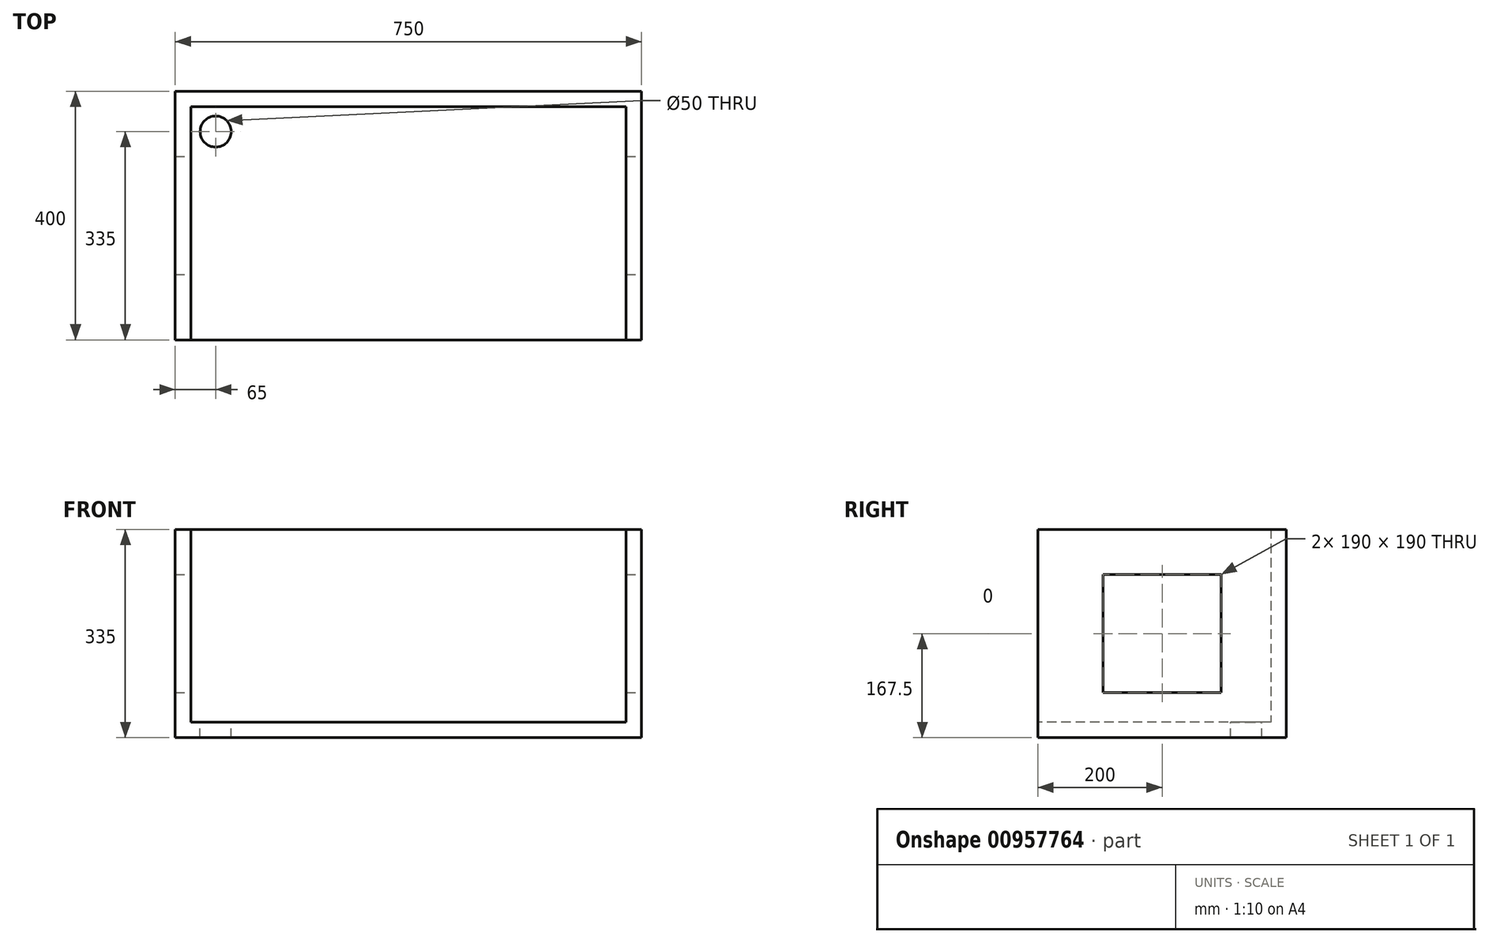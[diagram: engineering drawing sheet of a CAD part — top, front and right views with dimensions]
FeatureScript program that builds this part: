
annotation { "Feature Type Name" : "Feature", "Feature Type Description" : "" }
export const myFeature = defineFeature(function(context is Context, id is Id, definition is map)
    precondition{}
    {
        {
            var Q0;
            Q0=qCreatedBy(makeId("Top.planeOp"),FACE);
            var sketch = newSketch(context, id + "F0", { "sketchPlane" : qUnion([Q0])});
            skLineSegment(sketch, "E0.bottom", {"start": v(-375, 200) * mm, "end": v(375, 200) * mm});
            skLineSegment(sketch, "E0.top", {"start": v(-375, -200) * mm, "end": v(375, -200) * mm});
            skLineSegment(sketch, "E0.left", {"start": v(-375, 200) * mm, "end": v(-375, -200) * mm});
            skLineSegment(sketch, "E0.right", {"start": v(375, 200) * mm, "end": v(375, -200) * mm});
            skPoint(sketch, "E0.middle", {"position": v(0, 0) * mm});
            skSolve(sketch);
        }
        {
            var Q0;
            Q0=makeQuery(id+"F0.imprint","IMPRINT",FACE,{"disambiguationData":[TD([[makeQuery(id+"F0.imprint","IMPRINT",EDGE,{"derivedFrom":sQuery(id+"F0.wireOp",EDGE,"E0.bottom")}),-1.0]])]});
            extrude(context, id + "F1", {"entities" : qUnion([Q0]), "depth" : 25 * mm, "offsetDistance" : 25 * mm});
        }
        {
            var Q0;
            Q0=makeQuery(id+"F1.opExtrude","CAP_FACE",FACE,{"disambiguationData":[OSD([sQuery(id+"F0.wireOp",EDGE,"E0.bottom"),sQuery(id+"F0.wireOp",EDGE,"E0.top"),sQuery(id+"F0.wireOp",EDGE,"E0.left"),sQuery(id+"F0.wireOp",EDGE,"E0.right")])],"isStart":false});
            var sketch = newSketch(context, id + "F2", { "sketchPlane" : qUnion([Q0])});
            skLineSegment(sketch, "E1.0", {"start": v(-350, 175) * mm, "end": v(-350, -200) * mm});
            skLineSegment(sketch, "E2.0", {"start": v(-350, 175) * mm, "end": v(350, 175) * mm});
            skLineSegment(sketch, "E3.0", {"start": v(350, 175) * mm, "end": v(350, -200) * mm});
            skSolve(sketch);
        }
        {
            var Q0;
            {var subQ1=sQuery(id+"F2.wireOp",EDGE,"E1.0");Q0=makeQuery(id+"F2.imprint","IMPRINT",FACE,{"disambiguationData":[TD([[makeQuery(id+"F2.imprint","IMPRINT",EDGE,{"derivedFrom":subQ1}),-1.0]])]});}
            extrude(context, id + "F3", {"entities" : qUnion([Q0]), "operationType" : NewBodyOperationType.ADD, "depth" : 310 * mm, "offsetDistance" : 25 * mm});
        }
        {
            var Q0;
            {var subQ0=sQuery(id+"F0.wireOp",EDGE,"E0.right");Q0=makeQuery(id+"F3.boolean.opBoolean","MERGE",FACE,{"derivedFrom":[makeQuery(id+"F1.opExtrude","SWEPT_FACE",FACE,{"disambiguationData":[OSD([subQ0])]}),makeQuery(id+"F3.opExtrude","SWEPT_FACE",FACE,{"disambiguationData":[OSD([subQ0])]})]});}
            var sketch = newSketch(context, id + "F4", { "sketchPlane" : qUnion([Q0])});
            skLineSegment(sketch, "E4", {"start": v(-200, 335) * mm, "end": v(200, 0) * mm, "construction": true});
            skLineSegment(sketch, "E5.bottom", {"start": v(-95, 262.5) * mm, "end": v(95, 262.5) * mm});
            skLineSegment(sketch, "E5.top", {"start": v(-95, 72.5) * mm, "end": v(95, 72.5) * mm});
            skLineSegment(sketch, "E5.left", {"start": v(-95, 262.5) * mm, "end": v(-95, 72.5) * mm});
            skLineSegment(sketch, "E5.right", {"start": v(95, 262.5) * mm, "end": v(95, 72.5) * mm});
            skPoint(sketch, "E5.middle", {"position": v(0, 167.5) * mm});
            skSolve(sketch);
        }
        {
            var Q0;
            Q0=makeQuery(id+"F4.imprint","IMPRINT",FACE,{"disambiguationData":[TD([[makeQuery(id+"F4.imprint","IMPRINT",EDGE,{"derivedFrom":sQuery(id+"F4.wireOp",EDGE,"E5.bottom")}),-1.0]])]});
            extrude(context, id + "F5", {"entities" : qUnion([Q0]), "operationType" : NewBodyOperationType.REMOVE, "endBound" : BoundingType.THROUGH_ALL, "oppositeDirection" : true, "depth" : 25 * mm, "offsetDistance" : 25 * mm});
        }
        {
            var Q0;
            Q0=makeQuery(id+"F1.opExtrude","CAP_FACE",FACE,{"disambiguationData":[OSD([sQuery(id+"F0.wireOp",EDGE,"E0.bottom"),sQuery(id+"F0.wireOp",EDGE,"E0.top"),sQuery(id+"F0.wireOp",EDGE,"E0.left"),sQuery(id+"F0.wireOp",EDGE,"E0.right")])],"isStart":false});
            var sketch = newSketch(context, id + "F6", { "sketchPlane" : qUnion([Q0])});
            skCircle(sketch, "E6", {"center": v(-310, 135) * mm, "radius": 25 * mm});
            skSolve(sketch);
        }
        {
            var Q0;
            Q0=makeQuery(id+"F6.imprint","IMPRINT",FACE,{"disambiguationData":[TD([[makeQuery(id+"F6.imprint","IMPRINT",EDGE,{"derivedFrom":sQuery(id+"F6.wireOp",EDGE,"E6")}),1.0]])]});
            extrude(context, id + "F7", {"entities" : qUnion([Q0]), "operationType" : NewBodyOperationType.REMOVE, "endBound" : BoundingType.THROUGH_ALL, "oppositeDirection" : true, "depth" : 25 * mm, "offsetDistance" : 25 * mm});
        }
    });
